# Revit family: Wood_Lockers_Combination_Locks-Salsbury_Industries-46000R_Series-1_Wide_Units
name_source: partatom
category: Specialty Equipment
units: mm (PartAtom-declared; Revit-internal decimal feet)

## family parameters
Always vertical = Yes
Cut with Voids When Loaded = No
Enable Cutting in Views = No
Maintain Annotation Orientation = No
OmniClass Number = 23.40.00.00
OmniClass Title = Equipment and Furnishings
Part Type = Normal
Room Calculation Point = No
Round Connector Dimension = Use Diameter
Shared = No
Work Plane-Based = No

## types (6) — shared parameters
Assembly Code = C1030310
Base Material = Particle Board Industrial Grade - Salsbury Finish - Black Melamine Overlay
Default Elevation = 0.000"
Door Location D1 = Premier Locker Doors_Resettable Lock : Box Style Door for Six Foot High Locker
Hardware = Aluminum - Salsbury Finish - Black Satin
Individual Door Height = 11.802"
Interior Material = Textured Melamine - Salsbury Finish - White
Manufacturer = Salsbury Industries
MasterFormat Code = 10 51 23
MasterFormat Title = Lockers
OmniClass 23 Number = 23.40.00.00
OmniClass 23 Title = Equipment and Furnishings
Primary Structure Materials = Particle Board Industrial Grade - Salsbury Finish - Plain
Secondary Structure Materials = Particle Board Industrial Grade - Salsbury Finish - Black Melamine Overlay
Type Comments = Premier Wood Lockers - Box Style - Six Tier - with Resettable Combination Locks
URL = www.lockers.com
Unit Height = 72.000"
Width = 12.000"

## per-type parameters (varying)
| type | Base | Base Height | Depth | Description | Model | Sloping Hood Height | Version |
| 46165-R | Wood Locker Bases : Base - 12" W x 15" D Lockers | 4.000" | 15.000" | 1 Wide - 6 Feet High - 15 inches Deep - with Base | 46165-E | 5.743" | 1.0 (01/31/24) |
| 46165-R - without Base | Wood Locker Bases : None | 0.000" | 15.000" | 1 Wide - 6 Feet High - 15 inches Deep - without Base | 46165-R without Base | 5.743" | 1.0  (01/31/24) |
| 46168-R | Wood Locker Bases : Base - 12" W x 18" D Lockers | 4.000" | 18.000" | 1 Wide - 6 Feet High - 18 inches Deep - with Base | 46168-R | 6.868" | 1.0 (01/31/24) |
| 46168-R - without Base | Wood Locker Bases : None | 0.000" | 18.000" | 1 Wide - 6 Feet High - 18 inches Deep - without Base | 46168-R without Base | 6.868" | 1.0 (01/31/24) |
| 46161-R | Wood Locker Bases : Base - 12" W x 21" D Lockers | 4.000" | 21.000" | 1 Wide - 6 Feet High - 21 inches Deep - with Base | 46161-R | 7.993" | 1.0 (01/31/24) |
| 46161-R - without Base | Wood Locker Bases : None | 0.000" | 21.000" | 1 Wide - 6 Feet High - 21 inches Deep - without Base | 46161-R without Base | 7.993" | 1.0 (01/31/24) |

## geometry (parser evidence)
native form markers: Sweep x37
no freeform markers — native parametric forms only
